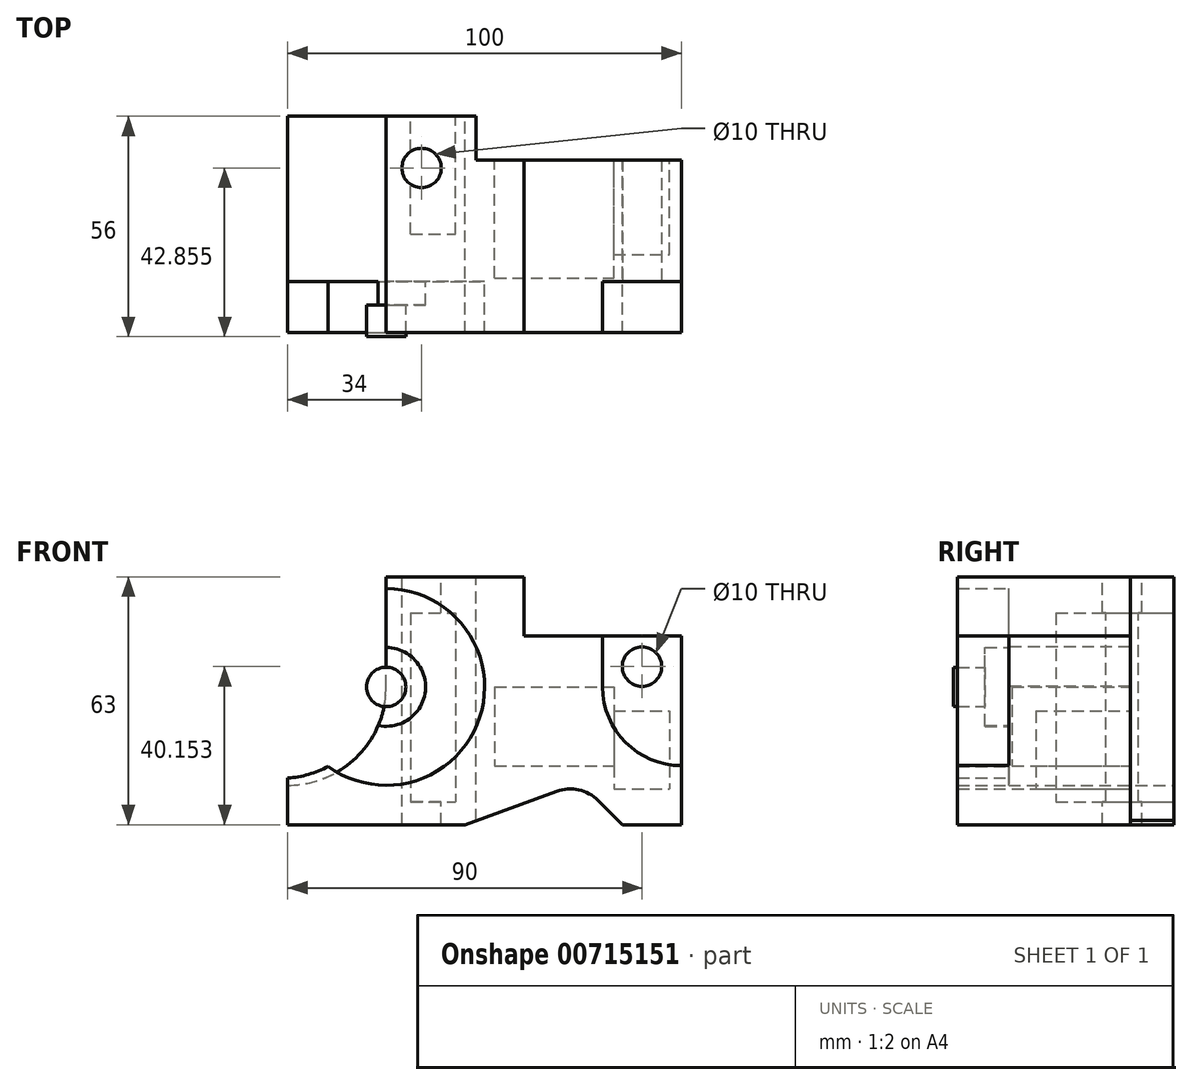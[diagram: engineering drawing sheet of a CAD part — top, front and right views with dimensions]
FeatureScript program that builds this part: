
annotation { "Feature Type Name" : "Feature", "Feature Type Description" : "" }
export const myFeature = defineFeature(function(context is Context, id is Id, definition is map)
    precondition{}
    {
        {
            var Q0;
            Q0=qCreatedBy(makeId("Front.planeOp"),FACE);
            var sketch = newSketch(context, id + "F0", { "sketchPlane" : qUnion([Q0])});
            skLineSegment(sketch, "E0", {"start": v(-25, -35) * mm, "end": v(20, -35) * mm});
            skLineSegment(sketch, "E1", {"start": v(20, -35) * mm, "end": v(43.34, -26.5) * mm});
            skLineSegment(sketch, "E2", {"start": v(53.83, -28.83) * mm, "end": v(60, -35) * mm});
            skLineSegment(sketch, "E3", {"start": v(60, -35) * mm, "end": v(75, -35) * mm});
            skLineSegment(sketch, "E4", {"start": v(75, -35) * mm, "end": v(75, 13) * mm});
            skLineSegment(sketch, "E5", {"start": v(75, 13) * mm, "end": v(35, 13) * mm});
            skLineSegment(sketch, "E6", {"start": v(35, 13) * mm, "end": v(35, 28) * mm});
            skLineSegment(sketch, "E7", {"start": v(35, 28) * mm, "end": v(0, 28) * mm});
            skLineSegment(sketch, "E8", {"start": v(-25, -35) * mm, "end": v(-25, -25) * mm});
            skArc(sketch, "E9", {"start": v(-25, -25) * mm, "mid": v(-7.32, -17.68) * mm, "end": v(0, 0) * mm});
            skLineSegment(sketch, "E10", {"start": v(0, 0) * mm, "end": v(0, 28) * mm});
            skLineSegment(sketch, "E11", {"start": v(20, -35) * mm, "end": v(60, -35) * mm});
            skPoint(sketch, "E12.visualSharp", {"position": v(49.33, -24.33) * mm});
            skArc(sketch, "E12.filletArc", {"start": v(53.83, -28.83) * mm, "mid": v(48.92, -26.14) * mm, "end": v(43.34, -26.5) * mm});
            skSolve(sketch);
        }
        {
            var Q0;
            Q0=makeQuery(id+"F0.imprint","IMPRINT",FACE,{"disambiguationData":[TD([[makeQuery(id+"F0.imprint","IMPRINT",EDGE,{"derivedFrom":sQuery(id+"F0.wireOp",EDGE,"E0")}),1.0]])]});
            extrude(context, id + "F1", {"entities" : qUnion([Q0]), "depth" : 42 * mm, "offsetDistance" : 25 * mm});
        }
        {
            var Q0;
            Q0=makeQuery(id+"F1.opExtrude","CAP_FACE",FACE,{"disambiguationData":[OSD([sQuery(id+"F0.wireOp",EDGE,"E0"),sQuery(id+"F0.wireOp",EDGE,"E1"),sQuery(id+"F0.wireOp",EDGE,"E2"),sQuery(id+"F0.wireOp",EDGE,"E3"),sQuery(id+"F0.wireOp",EDGE,"E4"),sQuery(id+"F0.wireOp",EDGE,"E5"),sQuery(id+"F0.wireOp",EDGE,"E6"),sQuery(id+"F0.wireOp",EDGE,"E7"),sQuery(id+"F0.wireOp",EDGE,"E8"),sQuery(id+"F0.wireOp",EDGE,"E9"),sQuery(id+"F0.wireOp",EDGE,"E10"),sQuery(id+"F0.wireOp",EDGE,"E12.filletArc")])],"isStart":false});
            var sketch = newSketch(context, id + "F2", { "sketchPlane" : qUnion([Q0])});
            skArc(sketch, "E13", {"start": v(-2, -9.8) * mm, "mid": v(9.95, -1) * mm, "end": v(0, 10) * mm});
            skLineSegment(sketch, "E14", {"start": v(0, 0) * mm, "end": v(0, 10) * mm});
            skArc(sketch, "E15", {"start": v(-2, -9.8) * mm, "mid": v(-0.5, -5) * mm, "end": v(0, 0) * mm});
            skSolve(sketch);
        }
        {
            var Q0;
            Q0 = qSketchRegion(id + "F2", true);
            extrude(context, id + "F3", {"entities" : qUnion([Q0]), "operationType" : NewBodyOperationType.ADD, "depth" : 6 * mm, "offsetDistance" : 25 * mm});
        }
        {
            var Q0;
            Q0=makeQuery(id+"F3.opExtrude","CAP_FACE",FACE,{"disambiguationData":[OSD([sQuery(id+"F2.wireOp",EDGE,"E13")])],"isStart":false});
            var sketch = newSketch(context, id + "F4", { "sketchPlane" : qUnion([Q0])});
            skCircle(sketch, "E16", {"center": v(0, 0) * mm, "radius": 5 * mm});
            skSolve(sketch);
        }
        {
            var Q0;
            Q0 = qSketchRegion(id + "F4", true);
            extrude(context, id + "F5", {"entities" : qUnion([Q0]), "operationType" : NewBodyOperationType.ADD, "depth" : 8 * mm, "offsetDistance" : 25 * mm});
        }
        {
            var Q0;
            Q0=makeQuery(id+"F1.opExtrude","CAP_FACE",FACE,{"disambiguationData":[OSD([sQuery(id+"F0.wireOp",EDGE,"E0"),sQuery(id+"F0.wireOp",EDGE,"E1"),sQuery(id+"F0.wireOp",EDGE,"E2"),sQuery(id+"F0.wireOp",EDGE,"E3"),sQuery(id+"F0.wireOp",EDGE,"E4"),sQuery(id+"F0.wireOp",EDGE,"E5"),sQuery(id+"F0.wireOp",EDGE,"E6"),sQuery(id+"F0.wireOp",EDGE,"E7"),sQuery(id+"F0.wireOp",EDGE,"E8"),sQuery(id+"F0.wireOp",EDGE,"E9"),sQuery(id+"F0.wireOp",EDGE,"E10"),sQuery(id+"F0.wireOp",EDGE,"E12.filletArc")])],"isStart":false});
            var sketch = newSketch(context, id + "F6", { "sketchPlane" : qUnion([Q0])});
            skArc(sketch, "E17", {"start": v(-14.73, -20.2) * mm, "mid": v(23.77, -7.75) * mm, "end": v(0, 25) * mm});
            skLineSegment(sketch, "E18", {"start": v(0, 25) * mm, "end": v(0, 28) * mm});
            skLineSegment(sketch, "E19", {"start": v(0, 28) * mm, "end": v(35, 28) * mm});
            skLineSegment(sketch, "E20", {"start": v(35, 28) * mm, "end": v(35, 13) * mm});
            skLineSegment(sketch, "E21", {"start": v(35, 13) * mm, "end": v(55, 13) * mm});
            skLineSegment(sketch, "E22", {"start": v(55, 13) * mm, "end": v(55, 0) * mm});
            skArc(sketch, "E23", {"start": v(55, 0) * mm, "mid": v(60.86, -14.14) * mm, "end": v(75, -20) * mm});
            skLineSegment(sketch, "E24", {"start": v(75, -20) * mm, "end": v(75, -35) * mm});
            skLineSegment(sketch, "E25", {"start": v(75, -35) * mm, "end": v(60, -35) * mm});
            skLineSegment(sketch, "E26", {"start": v(60, -35) * mm, "end": v(53.83, -28.83) * mm});
            skArc(sketch, "E27", {"start": v(53.83, -28.83) * mm, "mid": v(48.92, -26.14) * mm, "end": v(43.34, -26.5) * mm});
            skLineSegment(sketch, "E28", {"start": v(43.34, -26.5) * mm, "end": v(20, -35) * mm});
            skLineSegment(sketch, "E29", {"start": v(20, -35) * mm, "end": v(-25, -35) * mm});
            skLineSegment(sketch, "E30", {"start": v(-25, -35) * mm, "end": v(-25, -23.14) * mm});
            skArc(sketch, "E31", {"start": v(-25, -23.14) * mm, "mid": v(-19.7, -22.23) * mm, "end": v(-14.73, -20.2) * mm});
            skSolve(sketch);
        }
        {
            var Q0;
            Q0 = qSketchRegion(id + "F6", true);
            extrude(context, id + "F7", {"entities" : qUnion([Q0]), "operationType" : NewBodyOperationType.ADD, "depth" : 13 * mm, "offsetDistance" : 25 * mm});
        }
        {
            var Q0;
            {var subQ0=sQuery(id+"F0.wireOp",EDGE,"E5");var subQ1=sQuery(id+"F0.wireOp",EDGE,"E4");Q0=makeQuery(id+"F7.boolean.opBoolean","SPLIT",FACE,{"disambiguationData":[TD([makeQuery(id+"F1.opExtrude","SWEPT_FACE",FACE,{"disambiguationData":[OSD([subQ1])]})])],"derivedFrom":makeQuery(id+"F1.opExtrude","CAP_FACE",FACE,{"disambiguationData":[OSD([sQuery(id+"F0.wireOp",EDGE,"E0"),sQuery(id+"F0.wireOp",EDGE,"E1"),sQuery(id+"F0.wireOp",EDGE,"E2"),sQuery(id+"F0.wireOp",EDGE,"E3"),subQ1,subQ0,sQuery(id+"F0.wireOp",EDGE,"E6"),sQuery(id+"F0.wireOp",EDGE,"E7"),sQuery(id+"F0.wireOp",EDGE,"E8"),sQuery(id+"F0.wireOp",EDGE,"E9"),sQuery(id+"F0.wireOp",EDGE,"E10"),sQuery(id+"F0.wireOp",EDGE,"E12.filletArc")])],"isStart":false})});}
            var sketch = newSketch(context, id + "F8", { "sketchPlane" : qUnion([Q0])});
            skCircle(sketch, "E32", {"center": v(65, 5.15) * mm, "radius": 5 * mm});
            skSolve(sketch);
        }
        {
            var Q0;
            Q0 = qSketchRegion(id + "F8", true);
            extrude(context, id + "F9", {"entities" : qUnion([Q0]), "operationType" : NewBodyOperationType.REMOVE, "oppositeDirection" : true, "depth" : 100 * mm, "offsetDistance" : 25 * mm});
        }
        {
            var Q0;
            Q0=makeQuery(id+"F7.boolean.opBoolean","MERGE",FACE,{"derivedFrom":[makeQuery(id+"F1.opExtrude","SWEPT_FACE",FACE,{"disambiguationData":[OSD([sQuery(id+"F0.wireOp",EDGE,"E7")])]}),makeQuery(id+"F7.opExtrude","SWEPT_FACE",FACE,{"disambiguationData":[OSD([sQuery(id+"F6.wireOp",EDGE,"E19")])]})]});
            var sketch = newSketch(context, id + "F10", { "sketchPlane" : qUnion([Q0])});
            skLineSegment(sketch, "E33", {"start": v(22.88, 0) * mm, "end": v(22.88, -11.13) * mm});
            skLineSegment(sketch, "E34", {"start": v(22.88, -11.13) * mm, "end": v(77.8, -11.13) * mm});
            skLineSegment(sketch, "E35", {"start": v(77.8, -11.13) * mm, "end": v(77.8, 0) * mm});
            skLineSegment(sketch, "E36", {"start": v(77.8, 0) * mm, "end": v(22.88, 0) * mm});
            skSolve(sketch);
        }
        {
            var Q0;
            Q0 = qSketchRegion(id + "F10", true);
            extrude(context, id + "F11", {"entities" : qUnion([Q0]), "operationType" : NewBodyOperationType.REMOVE, "oppositeDirection" : true, "depth" : 100 * mm, "offsetDistance" : 25 * mm});
        }
        {
            var Q0;
            Q0=makeQuery(id+"F7.boolean.opBoolean","MERGE",FACE,{"derivedFrom":[makeQuery(id+"F1.opExtrude","SWEPT_FACE",FACE,{"disambiguationData":[OSD([sQuery(id+"F0.wireOp",EDGE,"E7")])]}),makeQuery(id+"F7.opExtrude","SWEPT_FACE",FACE,{"disambiguationData":[OSD([sQuery(id+"F6.wireOp",EDGE,"E19")])]})]});
            var sketch = newSketch(context, id + "F12", { "sketchPlane" : qUnion([Q0])});
            skCircle(sketch, "E37", {"center": v(9, -13.14) * mm, "radius": 5 * mm});
            skSolve(sketch);
        }
        {
            var Q0;
            Q0 = qSketchRegion(id + "F12", true);
            extrude(context, id + "F13", {"entities" : qUnion([Q0]), "operationType" : NewBodyOperationType.REMOVE, "oppositeDirection" : true, "depth" : 100 * mm, "offsetDistance" : 25 * mm});
        }
        {
            var Q0;
            Q0=makeQuery(id+"F11.boolean.opBoolean","COPY",FACE,{"derivedFrom":makeQuery(id+"F11.opExtrude","SWEPT_FACE",FACE,{"disambiguationData":[OSD([sQuery(id+"F10.wireOp",EDGE,"E34")])]})});
            var sketch = newSketch(context, id + "F14", { "sketchPlane" : qUnion([Q0])});
            skLineSegment(sketch, "E38.bottom", {"start": v(-27.54, 0) * mm, "end": v(-57.86, 0) * mm});
            skLineSegment(sketch, "E38.top", {"start": v(-27.54, -20.01) * mm, "end": v(-57.86, -20.01) * mm});
            skLineSegment(sketch, "E38.left", {"start": v(-27.54, 0) * mm, "end": v(-27.54, -20.01) * mm});
            skLineSegment(sketch, "E38.right", {"start": v(-57.86, 0) * mm, "end": v(-57.86, -20.01) * mm});
            skSolve(sketch);
        }
        {
            var Q0;
            Q0 = qSketchRegion(id + "F14", true);
            extrude(context, id + "F15", {"entities" : qUnion([Q0]), "operationType" : NewBodyOperationType.REMOVE, "oppositeDirection" : true, "depth" : 30 * mm, "offsetDistance" : 25 * mm});
        }
        {
            var Q0;
            Q0=makeQuery(id+"F1.opExtrude","CAP_FACE",FACE,{"disambiguationData":[OSD([sQuery(id+"F0.wireOp",EDGE,"E0"),sQuery(id+"F0.wireOp",EDGE,"E1"),sQuery(id+"F0.wireOp",EDGE,"E2"),sQuery(id+"F0.wireOp",EDGE,"E3"),sQuery(id+"F0.wireOp",EDGE,"E4"),sQuery(id+"F0.wireOp",EDGE,"E5"),sQuery(id+"F0.wireOp",EDGE,"E6"),sQuery(id+"F0.wireOp",EDGE,"E7"),sQuery(id+"F0.wireOp",EDGE,"E8"),sQuery(id+"F0.wireOp",EDGE,"E9"),sQuery(id+"F0.wireOp",EDGE,"E10"),sQuery(id+"F0.wireOp",EDGE,"E12.filletArc")])],"isStart":true});
            var sketch = newSketch(context, id + "F16", { "sketchPlane" : qUnion([Q0])});
            skLineSegment(sketch, "E39.bottom", {"start": v(-6.21, 18.8) * mm, "end": v(-17.66, 18.8) * mm});
            skLineSegment(sketch, "E39.top", {"start": v(-6.21, -29.15) * mm, "end": v(-17.66, -29.15) * mm});
            skLineSegment(sketch, "E39.left", {"start": v(-6.21, 18.8) * mm, "end": v(-6.21, -29.15) * mm});
            skLineSegment(sketch, "E39.right", {"start": v(-17.66, 18.8) * mm, "end": v(-17.66, -29.15) * mm});
            skSolve(sketch);
        }
        {
            var Q0;
            Q0 = qSketchRegion(id + "F16", true);
            extrude(context, id + "F17", {"entities" : qUnion([Q0]), "operationType" : NewBodyOperationType.REMOVE, "oppositeDirection" : true, "depth" : 30 * mm, "offsetDistance" : 25 * mm});
        }
        {
            var Q0;
            Q0=makeQuery(id+"F11.boolean.opBoolean","COPY",FACE,{"derivedFrom":makeQuery(id+"F11.opExtrude","SWEPT_FACE",FACE,{"disambiguationData":[OSD([sQuery(id+"F10.wireOp",EDGE,"E34")])]})});
            var sketch = newSketch(context, id + "F18", { "sketchPlane" : qUnion([Q0])});
            skLineSegment(sketch, "E40.bottom", {"start": v(-57.86, -6.16) * mm, "end": v(-72, -6.16) * mm});
            skLineSegment(sketch, "E40.top", {"start": v(-57.86, -25.96) * mm, "end": v(-72, -25.96) * mm});
            skLineSegment(sketch, "E40.left", {"start": v(-57.86, -6.16) * mm, "end": v(-57.86, -25.96) * mm});
            skLineSegment(sketch, "E40.right", {"start": v(-72, -6.16) * mm, "end": v(-72, -25.96) * mm});
            skSolve(sketch);
        }
        {
            var Q0;
            Q0 = qSketchRegion(id + "F18", true);
            extrude(context, id + "F19", {"entities" : qUnion([Q0]), "operationType" : NewBodyOperationType.REMOVE, "oppositeDirection" : true, "depth" : 24 * mm, "offsetDistance" : 25 * mm});
        }
    });
